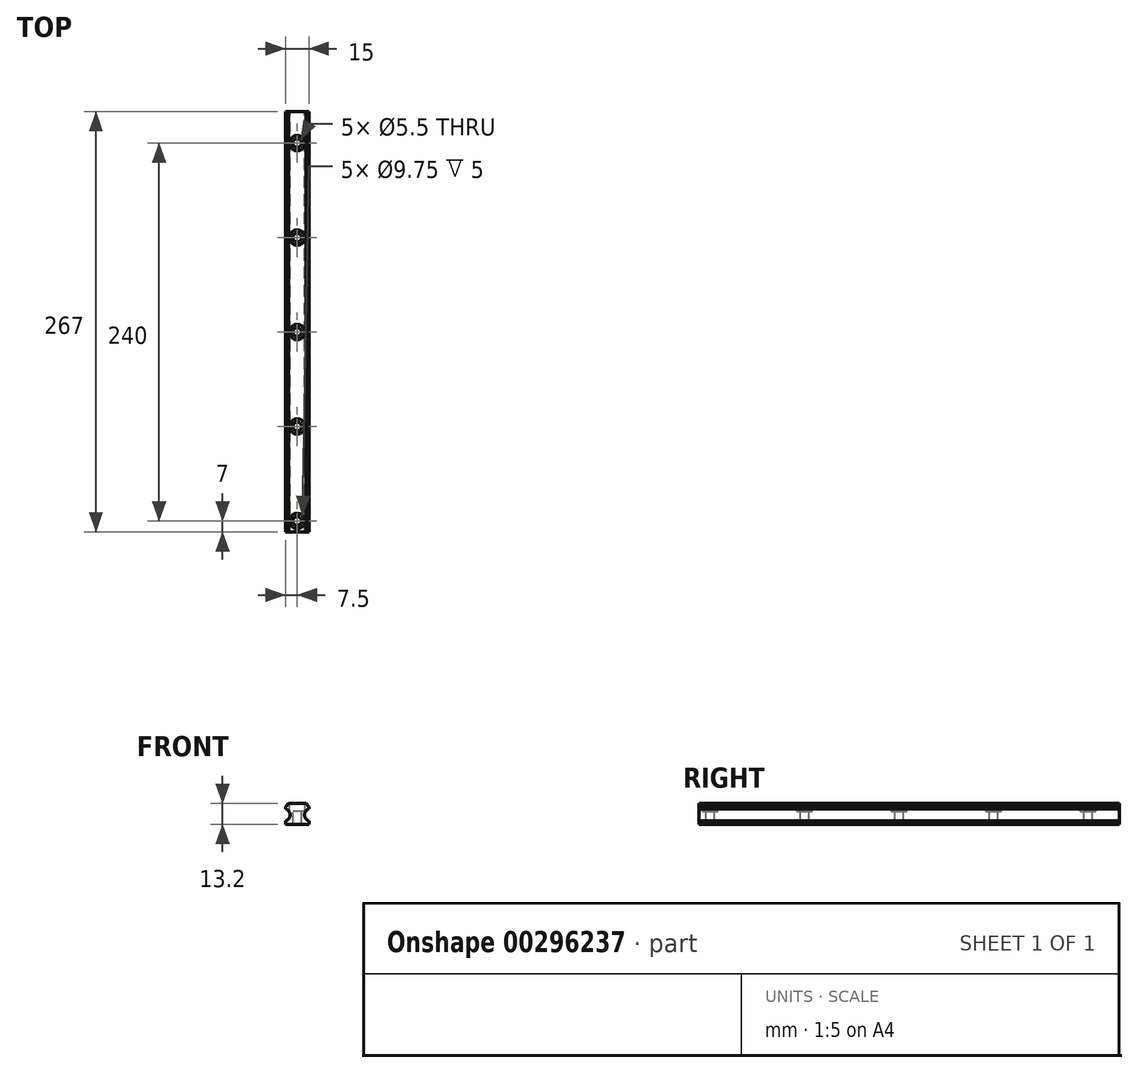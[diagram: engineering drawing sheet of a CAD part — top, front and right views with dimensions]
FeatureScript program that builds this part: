
annotation { "Feature Type Name" : "Feature", "Feature Type Description" : "" }
export const myFeature = defineFeature(function(context is Context, id is Id, definition is map)
    precondition{}
    {
        {
            var Q0;
            Q0=qCreatedBy(makeId("Front.planeOp"),FACE);
            var sketch = newSketch(context, id + "F0", { "sketchPlane" : qUnion([Q0])});
            skLineSegment(sketch, "E0", {"start": v(0, 0) * mm, "end": v(0, 42.87) * mm, "construction": true});
            skLineSegment(sketch, "E1.bottom", {"start": v(-7.5, 0) * mm, "end": v(7.5, 0) * mm});
            skLineSegment(sketch, "E1.top", {"start": v(-5.5, 13.2) * mm, "end": v(5.5, 13.2) * mm});
            skLineSegment(sketch, "E1.left", {"start": v(-7.5, 0) * mm, "end": v(-7.5, 2.15) * mm});
            skLineSegment(sketch, "E1.right", {"start": v(7.5, 0) * mm, "end": v(7.5, 2.15) * mm});
            skArc(sketch, "E2", {"start": v(-7.5, 2.15) * mm, "mid": v(-4.6, 6) * mm, "end": v(-7.5, 9.85) * mm});
            skArc(sketch, "E3", {"start": v(7.5, 9.85) * mm, "mid": v(4.6, 6) * mm, "end": v(7.5, 2.15) * mm});
            skLineSegment(sketch, "E4.trimOffspring", {"start": v(7.5, 9.85) * mm, "end": v(7.5, 11.2) * mm});
            skLineSegment(sketch, "E5.trimOffspring", {"start": v(-7.5, 9.85) * mm, "end": v(-7.5, 11.2) * mm});
            skLineSegment(sketch, "E6", {"start": v(-7.5, 11.2) * mm, "end": v(-5.5, 13.2) * mm});
            skLineSegment(sketch, "E7", {"start": v(5.5, 13.2) * mm, "end": v(7.5, 11.2) * mm});
            skSolve(sketch);
        }
        {
            var Q0;
            Q0=qSketchRegion(id+"F0",true);
            extrude(context, id + "F1", {"entities" : qUnion([Q0]), "depth" : 460 * mm});
        }
        {
            var Q0;
            Q0=makeQuery(id+"F1.opExtrude","SWEPT_FACE",FACE,{"disambiguationData":[OSD([sQuery(id+"F0.wireOp",EDGE,"E1.top")])]});
            var sketch = newSketch(context, id + "F2", { "sketchPlane" : qUnion([Q0])});
            skLineSegment(sketch, "E8", {"start": v(0, 0) * mm, "end": v(0, -460) * mm, "construction": true});
            skPoint(sketch, "E9", {"position": v(0, -440) * mm});
            skPoint(sketch, "E10.0.1.0", {"position": v(0, -380) * mm});
            skPoint(sketch, "E10.0.2.0", {"position": v(0, -320) * mm});
            skPoint(sketch, "E10.0.3.0", {"position": v(0, -260) * mm});
            skPoint(sketch, "E10.0.4.0", {"position": v(0, -200) * mm});
            skPoint(sketch, "E10.0.5.0", {"position": v(0, -140) * mm});
            skPoint(sketch, "E10.0.6.0", {"position": v(0, -80) * mm});
            skPoint(sketch, "E10.0.7.0", {"position": v(0, -20) * mm});
            skLineSegment(sketch, "E10.direction1", {"start": v(0, -440) * mm, "end": v(25, -440) * mm, "construction": true});
            skLineSegment(sketch, "E10.direction2", {"start": v(0, -440) * mm, "end": v(0, -380) * mm, "construction": true});
            skSolve(sketch);
        }
        {
            var Q0;
            Q0=sQuery(id+"F2.wireOp",VERTEX,"E10.0.7.0");
            var Q1;
            Q1=sQuery(id+"F2.wireOp",VERTEX,"E10.0.6.0");
            var Q2;
            Q2=sQuery(id+"F2.wireOp",VERTEX,"E10.0.5.0");
            var Q3;
            Q3=sQuery(id+"F2.wireOp",VERTEX,"E10.0.4.0");
            var Q4;
            Q4=sQuery(id+"F2.wireOp",VERTEX,"E10.0.3.0");
            var Q5;
            Q5=sQuery(id+"F2.wireOp",VERTEX,"E10.0.2.0");
            var Q6;
            Q6=sQuery(id+"F2.wireOp",VERTEX,"E10.0.1.0");
            var Q7;
            Q7=sQuery(id+"F2.wireOp",VERTEX,"E9");
            var Q8;
            Q8=makeQuery(id+"F1.opExtrude","SWEPT_BODY",BODY,{"disambiguationData":[OSD([sQuery(id+"F0.wireOp",EDGE,"E1.bottom"),sQuery(id+"F0.wireOp",EDGE,"E1.top"),sQuery(id+"F0.wireOp",EDGE,"E1.left"),sQuery(id+"F0.wireOp",EDGE,"E1.right"),sQuery(id+"F0.wireOp",EDGE,"E2"),sQuery(id+"F0.wireOp",EDGE,"E3"),sQuery(id+"F0.wireOp",EDGE,"E4.trimOffspring"),sQuery(id+"F0.wireOp",EDGE,"E5.trimOffspring"),sQuery(id+"F0.wireOp",EDGE,"E6"),sQuery(id+"F0.wireOp",EDGE,"E7")])]});
            hole(context, id + "F3", {"style" : HoleStyle.C_BORE, "endStyle" : HoleEndStyle.THROUGH, "standardTappedOrClearance" : lookupTablePath({ "standard" : "ISO", "fit" : "Normal", "size" : "M5", "type" : "Clearance" }), "standardBlindInLast" : lookupTablePath({ "fit" : "Standard", "standard" : "ISO", "size" : "M5", "type" : "Clearance" }), "holeDiameter" : 5.5 * mm, "cBoreDiameter" : 9.75 * mm, "cBoreDepth" : 5 * mm, "tappedDepth" : 12 * mm, "tapClearance" : 3, "locations" : qUnion([Q0, Q1, Q2, Q3, Q4, Q5, Q6, Q7]), "scope" : qUnion([Q8])});
        }
        {
            var Q0;
            Q0=makeQuery(id+"F1.opExtrude","SWEPT_FACE",FACE,{"disambiguationData":[OSD([sQuery(id+"F0.wireOp",EDGE,"E1.bottom")])]});
            var sketch = newSketch(context, id + "F4", { "sketchPlane" : qUnion([Q0])});
            skLineSegment(sketch, "E11.bottom", {"start": v(-30, 460) * mm, "end": v(30, 460) * mm});
            skLineSegment(sketch, "E11.top", {"start": v(-30, 267) * mm, "end": v(30, 267) * mm});
            skLineSegment(sketch, "E11.left", {"start": v(-30, 460) * mm, "end": v(-30, 267) * mm});
            skLineSegment(sketch, "E11.right", {"start": v(30, 460) * mm, "end": v(30, 267) * mm});
            skLineSegment(sketch, "E12", {"start": v(0, 0) * mm, "end": v(0, 460) * mm, "construction": true});
            skSolve(sketch);
        }
        {
            var Q0;
            Q0=qSketchRegion(id+"F4",true);
            extrude(context, id + "F5", {"entities" : qUnion([Q0]), "operationType" : NewBodyOperationType.REMOVE, "endBound" : BoundingType.THROUGH_ALL, "oppositeDirection" : true, "depth" : 25 * mm});
        }
    });
